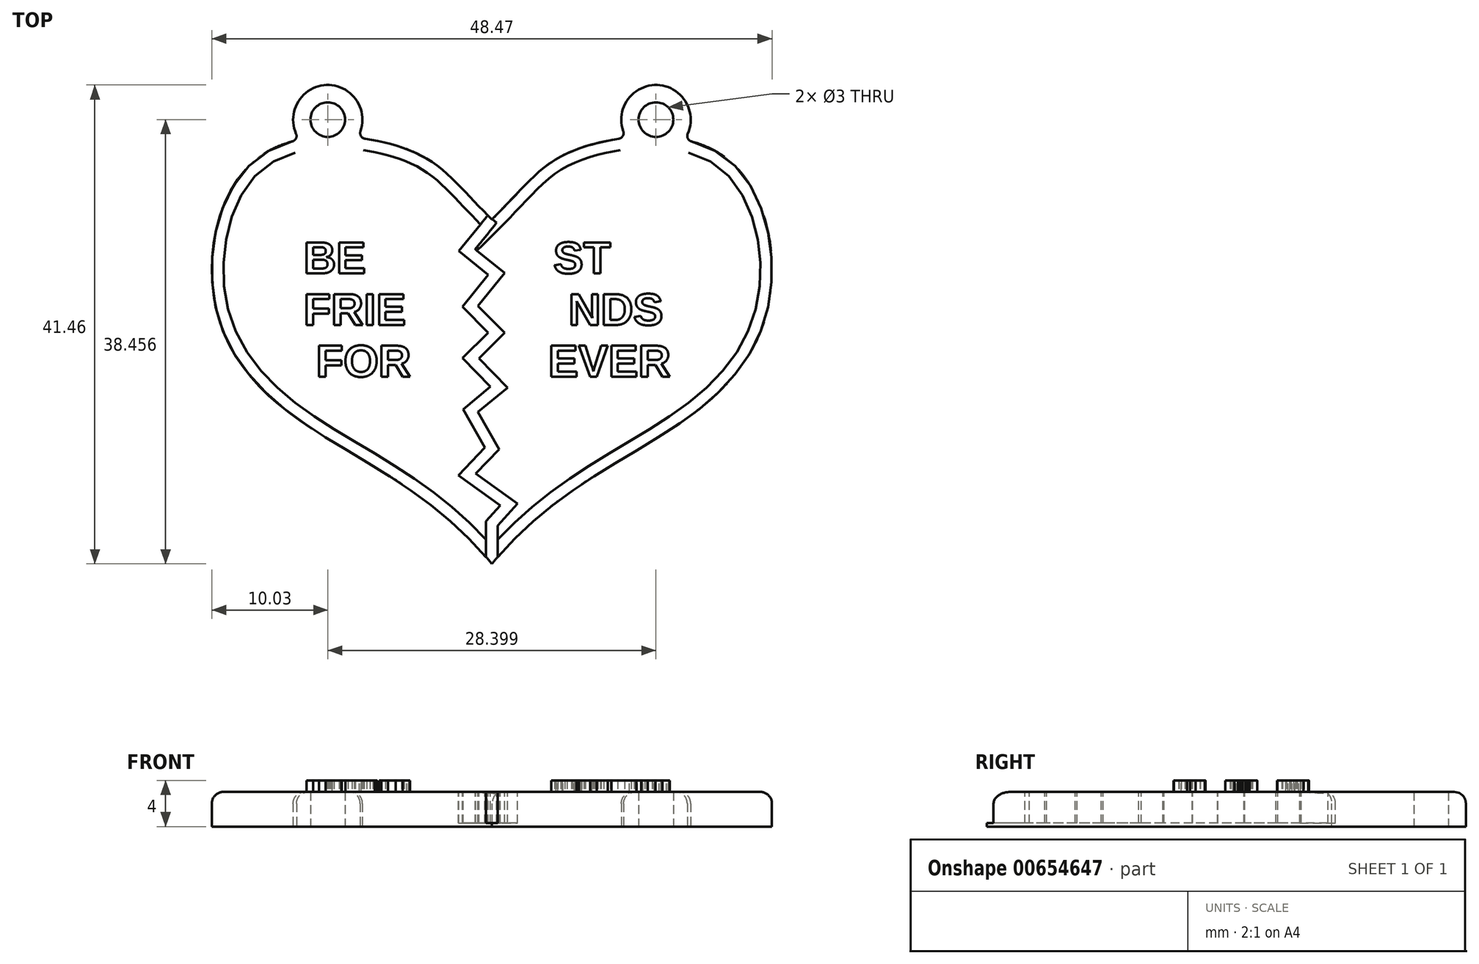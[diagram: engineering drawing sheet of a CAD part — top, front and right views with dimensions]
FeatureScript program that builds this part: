
annotation { "Feature Type Name" : "Feature", "Feature Type Description" : "" }
export const myFeature = defineFeature(function(context is Context, id is Id, definition is map)
    precondition{}
    {
        {
            var Q0;
            Q0=qCreatedBy(makeId("Top.planeOp"),FACE);
            var sketch = newSketch(context, id + "F0", { "sketchPlane" : qUnion([Q0])});
            skLineSegment(sketch, "E0", {"start": v(0, 0) * mm, "end": v(0, 29.81) * mm, "construction": true});
            skFitSpline(sketch, "E1", {"points": [v(0, 29.81) * mm, v(-7.06, 35.77) * mm, v(-19.86, 35.42) * mm, v(-24.03, 22.92) * mm, v(-16.98, 12.67) * mm, v(0, 0) * mm], "startDerivative": vector(-58.04, 58.16) * mm, "endDerivative": vector(65.78, -79.51) * mm});
            skFitSpline(sketch, "E2.MirrorCS", {"points": [v(0, 29.81) * mm, v(7.06, 35.77) * mm, v(19.86, 35.42) * mm, v(24.03, 22.92) * mm, v(16.98, 12.67) * mm, v(0, 0) * mm], "startDerivative": vector(58.04, 58.16) * mm, "endDerivative": vector(-65.78, -79.51) * mm});
            skArc(sketch, "E3", {"start": v(-11.37, 37.46) * mm, "mid": v(-14.31, 41.45) * mm, "end": v(-16.95, 37.25) * mm});
            skFitSpline(sketch, "E4.trimOffspring", {"points": [v(0, 29.81) * mm, v(-7.06, 35.77) * mm, v(-19.86, 35.42) * mm, v(-24.03, 22.92) * mm, v(-16.98, 12.67) * mm, v(0, 0) * mm], "startDerivative": vector(-58.04, 58.16) * mm, "endDerivative": vector(65.78, -79.51) * mm});
            skCircle(sketch, "E5", {"center": v(-14.2, 38.46) * mm, "radius": 1.5 * mm});
            skArc(sketch, "E6.MirrorCS", {"start": v(11.37, 37.46) * mm, "mid": v(14.31, 41.45) * mm, "end": v(16.95, 37.25) * mm});
            skCircle(sketch, "E7", {"center": v(14.2, 38.46) * mm, "radius": 1.5 * mm});
            skPoint(sketch, "E8.visualSharp", {"position": v(-16.64, 36.72) * mm});
            skArc(sketch, "E8.filletArc", {"start": v(-17.27, 36.56) * mm, "mid": v(-16.95, 36.83) * mm, "end": v(-16.95, 37.25) * mm});
            skPoint(sketch, "E9.visualSharp", {"position": v(-11.64, 36.89) * mm});
            skArc(sketch, "E9.filletArc", {"start": v(-11.37, 37.46) * mm, "mid": v(-11.33, 37.03) * mm, "end": v(-10.97, 36.8) * mm});
            skPoint(sketch, "E10.visualSharp", {"position": v(11.64, 36.89) * mm});
            skArc(sketch, "E10.filletArc", {"start": v(10.97, 36.8) * mm, "mid": v(11.33, 37.03) * mm, "end": v(11.37, 37.46) * mm});
            skPoint(sketch, "E11.visualSharp", {"position": v(16.64, 36.72) * mm});
            skArc(sketch, "E11.filletArc", {"start": v(16.95, 37.25) * mm, "mid": v(16.95, 36.83) * mm, "end": v(17.27, 36.56) * mm});
            skSolve(sketch);
        }
        {
            var Q0;
            Q0 = qSketchRegion(id + "F0", true);
            extrude(context, id + "F1", {"entities" : qUnion([Q0]), "depth" : 3 * mm, "offsetDistance" : 25 * mm});
        }
        {
            var Q0;
            Q0=makeQuery(id+"F1.opExtrude","CAP_FACE",FACE,{"disambiguationData":[OSD([sQuery(id+"F0.wireOp",EDGE,"E1"),sQuery(id+"F0.wireOp",EDGE,"E2.MirrorCS")])],"isStart":false});
            var sketch = newSketch(context, id + "F2", { "sketchPlane" : qUnion([Q0])});
            skLineSegment(sketch, "E12", {"start": v(0, 29.81) * mm, "end": v(-2.15, 27.15) * mm, "construction": true});
            skLineSegment(sketch, "E13", {"start": v(-2.15, 27.15) * mm, "end": v(0.39, 25.1) * mm, "construction": true});
            skLineSegment(sketch, "E14", {"start": v(0.39, 25.1) * mm, "end": v(-1.88, 22.3) * mm, "construction": true});
            skLineSegment(sketch, "E15", {"start": v(-1.88, 22.3) * mm, "end": v(0.39, 20) * mm, "construction": true});
            skLineSegment(sketch, "E16", {"start": v(0.39, 20) * mm, "end": v(-1.83, 17.8) * mm, "construction": true});
            skLineSegment(sketch, "E17", {"start": v(-1.83, 17.8) * mm, "end": v(0.6, 15.3) * mm, "construction": true});
            skLineSegment(sketch, "E18", {"start": v(0.6, 15.3) * mm, "end": v(-1.84, 13.26) * mm, "construction": true});
            skLineSegment(sketch, "E19", {"start": v(-1.84, 13.26) * mm, "end": v(0, 9.99) * mm, "construction": true});
            skLineSegment(sketch, "E20", {"start": v(0, 9.99) * mm, "end": v(-2.15, 7.73) * mm, "construction": true});
            skLineSegment(sketch, "E21", {"start": v(-2.15, 7.73) * mm, "end": v(1.46, 5.11) * mm, "construction": true});
            skLineSegment(sketch, "E22", {"start": v(1.46, 5.11) * mm, "end": v(0, 3.48) * mm, "construction": true});
            skLineSegment(sketch, "E23", {"start": v(0, 29.81) * mm, "end": v(0, 3.48) * mm, "construction": true});
            skLineSegment(sketch, "E24.0", {"start": v(-0.5, 3.68) * mm, "end": v(-0.5, 0) * mm});
            skLineSegment(sketch, "E24.1", {"start": v(0.72, 5.04) * mm, "end": v(-0.5, 3.68) * mm});
            skLineSegment(sketch, "E24.2", {"start": v(-2.55, 22.26) * mm, "end": v(-0.32, 20) * mm});
            skLineSegment(sketch, "E24.3", {"start": v(-0.32, 25.03) * mm, "end": v(-2.55, 22.26) * mm});
            skLineSegment(sketch, "E24.4", {"start": v(-2.85, 27.07) * mm, "end": v(-0.32, 25.03) * mm});
            skLineSegment(sketch, "E24.5", {"start": v(-0.4, 30.1) * mm, "end": v(-2.85, 27.07) * mm});
            skLineSegment(sketch, "E24.6", {"start": v(-0.32, 20) * mm, "end": v(-2.54, 17.81) * mm});
            skLineSegment(sketch, "E24.7", {"start": v(-2.54, 17.81) * mm, "end": v(-0.13, 15.33) * mm});
            skLineSegment(sketch, "E24.8", {"start": v(-0.13, 15.33) * mm, "end": v(-2.48, 13.38) * mm});
            skLineSegment(sketch, "E24.9", {"start": v(-2.48, 13.38) * mm, "end": v(-0.62, 10.06) * mm});
            skLineSegment(sketch, "E24.10", {"start": v(-0.62, 10.06) * mm, "end": v(-2.9, 7.66) * mm});
            skLineSegment(sketch, "E24.11", {"start": v(-2.9, 7.66) * mm, "end": v(0.72, 5.04) * mm});
            skLineSegment(sketch, "E25.0", {"start": v(0.5, 3.3) * mm, "end": v(0.5, 0) * mm});
            skLineSegment(sketch, "E25.1", {"start": v(2.2, 5.2) * mm, "end": v(0.5, 3.3) * mm});
            skLineSegment(sketch, "E25.2", {"start": v(-1.2, 22.33) * mm, "end": v(1.1, 19.99) * mm});
            skLineSegment(sketch, "E25.3", {"start": v(1.1, 25.18) * mm, "end": v(-1.2, 22.33) * mm});
            skLineSegment(sketch, "E25.4", {"start": v(-1.44, 27.23) * mm, "end": v(1.1, 25.18) * mm});
            skLineSegment(sketch, "E25.5", {"start": v(0.4, 29.52) * mm, "end": v(-1.44, 27.23) * mm});
            skLineSegment(sketch, "E25.6", {"start": v(1.1, 19.99) * mm, "end": v(-1.13, 17.8) * mm});
            skLineSegment(sketch, "E25.7", {"start": v(-1.13, 17.8) * mm, "end": v(1.35, 15.25) * mm});
            skLineSegment(sketch, "E25.8", {"start": v(1.35, 15.25) * mm, "end": v(-1.2, 13.14) * mm});
            skLineSegment(sketch, "E25.9", {"start": v(-1.2, 13.14) * mm, "end": v(0.62, 9.9) * mm});
            skLineSegment(sketch, "E25.10", {"start": v(0.62, 9.9) * mm, "end": v(-1.4, 7.8) * mm});
            skLineSegment(sketch, "E25.11", {"start": v(-1.4, 7.8) * mm, "end": v(2.2, 5.2) * mm});
            skLineSegment(sketch, "E26", {"start": v(-0.4, 30.1) * mm, "end": v(-0.35, 30.17) * mm});
            skLineSegment(sketch, "E27", {"start": v(-0.5, 0) * mm, "end": v(0.5, 0) * mm});
            skLineSegment(sketch, "E28", {"start": v(0.4, 29.52) * mm, "end": v(-0.35, 30.17) * mm});
            skSolve(sketch);
        }
        {
            var Q0;
            {var subQ5=sQuery(id+"F2.wireOp",EDGE,"E24.1");Q0=makeQuery(id+"F2.imprint","IMPRINT",FACE,{"disambiguationData":[TD([[makeQuery(id+"F2.imprint","IMPRINT",EDGE,{"derivedFrom":subQ5}),1.0]])]});}
            extrude(context, id + "F3", {"entities" : qUnion([Q0]), "operationType" : NewBodyOperationType.REMOVE, "oppositeDirection" : true, "depth" : 2.7 * mm, "offsetDistance" : 25 * mm});
        }
        {
            var Q0;
            Q0=makeQuery(id+"F1.opExtrude","CAP_EDGE",EDGE,{"disambiguationData":[OSD([sQuery(id+"F0.wireOp",EDGE,"E1")])],"isStart":false});
            var Q1;
            Q1=makeQuery(id+"F1.opExtrude","CAP_EDGE",EDGE,{"disambiguationData":[OSD([sQuery(id+"F0.wireOp",EDGE,"E2.MirrorCS")])],"isStart":false});
            fillet(context, id + "F4", {"entities" : qUnion([Q0, Q1]), "radius" : 1 * mm, "tangentPropagation" : true, "allowEdgeOverflow" : false});
        }
        {
            var Q0;
            {var subQ0=sQuery(id+"F0.wireOp",EDGE,"E1");Q0=makeQuery(id+"F3.boolean.opBoolean","SPLIT",FACE,{"disambiguationData":[TD([makeQuery(id+"F1.opExtrude","SWEPT_FACE",FACE,{"disambiguationData":[OSD([subQ0])]})])],"derivedFrom":makeQuery(id+"F1.opExtrude","CAP_FACE",FACE,{"disambiguationData":[OSD([subQ0,sQuery(id+"F0.wireOp",EDGE,"E2.MirrorCS")])],"isStart":false})});}
            var sketch = newSketch(context, id + "F5", { "sketchPlane" : qUnion([Q0])});
            skText(sketch, "E29", { "text": "BE               ST\nFRIE             NDS\n FOR           EVER", "fontName": "Arimo-Bold.ttf"});
            const initialGuessF5  = {"E29": [-0.01629, 0.02515, 1, 0, 0.0028]};
            skSetInitialGuess(sketch, initialGuessF5);
            skSolve(sketch);
        }
        {
            var Q0;
            Q0 = qSketchRegion(id + "F5", true);
            extrude(context, id + "F6", {"entities" : qUnion([Q0]), "operationType" : NewBodyOperationType.ADD, "depth" : 1 * mm, "offsetDistance" : 25 * mm});
        }
    });
